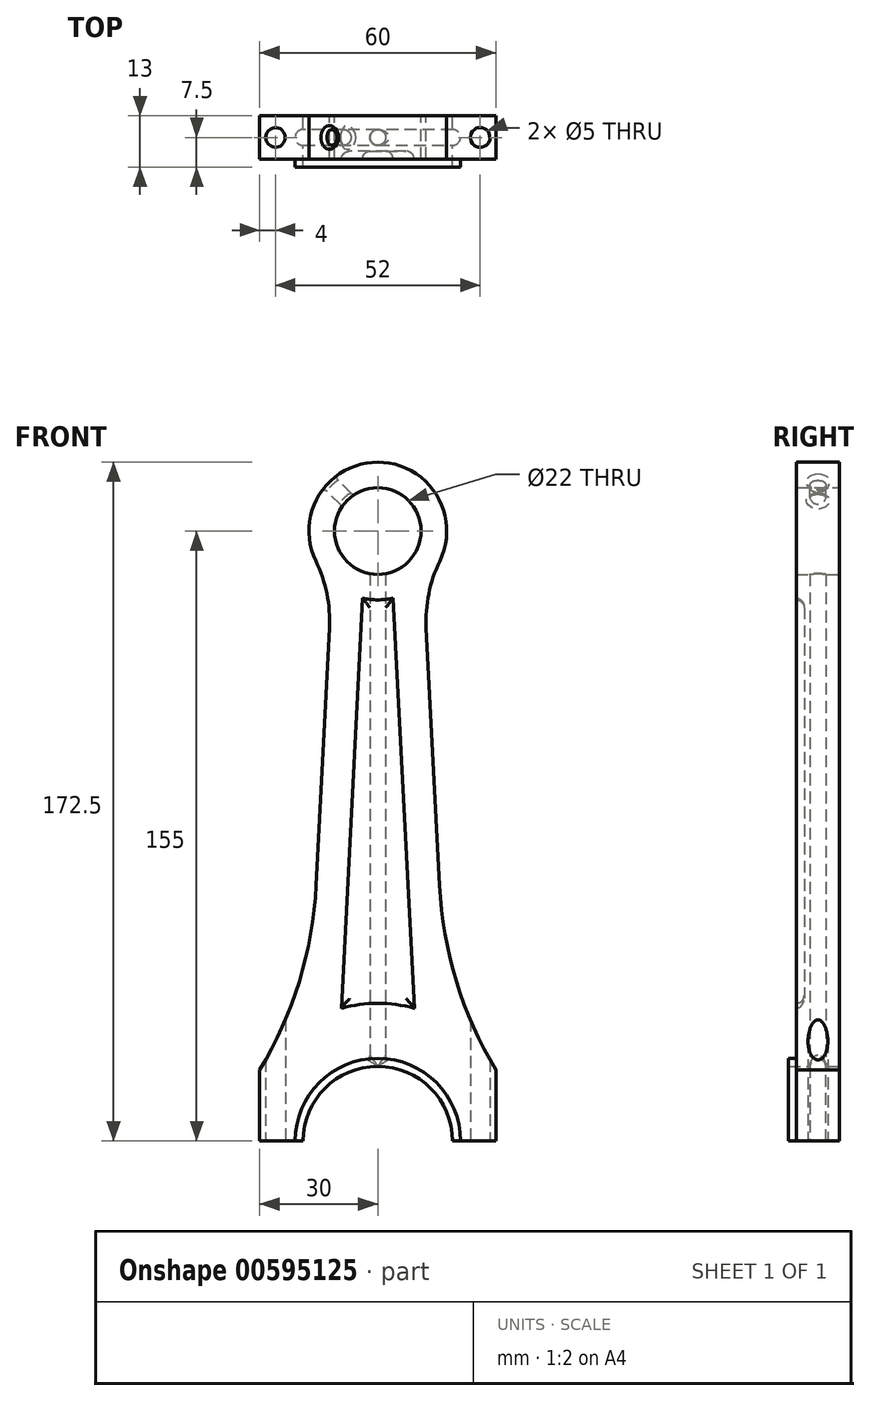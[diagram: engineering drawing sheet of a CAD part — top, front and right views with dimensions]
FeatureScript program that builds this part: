
annotation { "Feature Type Name" : "Feature", "Feature Type Description" : "" }
export const myFeature = defineFeature(function(context is Context, id is Id, definition is map)
    precondition{}
    {
        {
            var Q0;
            Q0=qCreatedBy(makeId("Front.planeOp"),FACE);
            var sketch = newSketch(context, id + "F0", { "sketchPlane" : qUnion([Q0])});
            skCircle(sketch, "E0", {"center": v(0, 77.5) * mm, "radius": 11 * mm});
            skArc(sketch, "E1", {"start": v(19, -77.5) * mm, "mid": v(0, -58.5) * mm, "end": v(-19, -77.5) * mm});
            skLineSegment(sketch, "E2", {"start": v(-12.3, 52.8) * mm, "end": v(-15.67, -12.54) * mm});
            skArc(sketch, "E3", {"start": v(15.75, 69.87) * mm, "mid": v(0, 95) * mm, "end": v(-15.75, 69.87) * mm});
            skLineSegment(sketch, "E4.trimOffspring", {"start": v(12.3, 52.8) * mm, "end": v(15.67, -12.54) * mm});
            skLineSegment(sketch, "E5", {"start": v(30, -59.47) * mm, "end": v(30, -77.5) * mm});
            skLineSegment(sketch, "E6.MirrorCS", {"start": v(-30, -59.47) * mm, "end": v(-30, -77.5) * mm});
            skLineSegment(sketch, "E7", {"start": v(0, -77.5) * mm, "end": v(-59.42, -77.5) * mm, "construction": true});
            skLineSegment(sketch, "E8.MirrorCS", {"start": v(0, -77.5) * mm, "end": v(59.42, -77.5) * mm, "construction": true});
            skLineSegment(sketch, "E9.trimOffspring", {"start": v(-30, -59.47) * mm, "end": v(-30, -59.47) * mm});
            skPoint(sketch, "E10.visualSharp", {"position": v(-17.46, -47.16) * mm});
            skArc(sketch, "E10.filletArc", {"start": v(-30, -59.47) * mm, "mid": v(-19.95, -36.89) * mm, "end": v(-15.67, -12.54) * mm});
            skArc(sketch, "E11.MirrorCS", {"start": v(30, -59.47) * mm, "mid": v(19.95, -36.89) * mm, "end": v(15.67, -12.54) * mm});
            skPoint(sketch, "E12.visualSharp", {"position": v(-11.69, 64.48) * mm});
            skArc(sketch, "E12.filletArc", {"start": v(-12.3, 52.8) * mm, "mid": v(-12.94, 61.55) * mm, "end": v(-15.75, 69.87) * mm});
            skPoint(sketch, "E13.visualSharp", {"position": v(11.69, 64.48) * mm});
            skArc(sketch, "E13.filletArc", {"start": v(15.75, 69.87) * mm, "mid": v(12.94, 61.55) * mm, "end": v(12.3, 52.8) * mm});
            skLineSegment(sketch, "E14", {"start": v(-30, -77.5) * mm, "end": v(-19, -77.5) * mm});
            skLineSegment(sketch, "E15", {"start": v(19, -77.5) * mm, "end": v(30, -77.5) * mm});
            skSolve(sketch);
        }
        {
            var Q0;
            Q0 = qSketchRegion(id + "F0", true);
            extrude(context, id + "F1", {"entities" : qUnion([Q0]), "endBound" : BoundingType.SYMMETRIC, "depth" : 11 * mm, "offsetDistance" : 25 * mm});
        }
        {
            var Q0;
            Q0=makeQuery(id+"F1.opExtrude","CAP_FACE",FACE,{"disambiguationData":[OSD([sQuery(id+"F0.wireOp",EDGE,"E0"),sQuery(id+"F0.wireOp",EDGE,"E1"),sQuery(id+"F0.wireOp",EDGE,"E2"),sQuery(id+"F0.wireOp",EDGE,"E3"),sQuery(id+"F0.wireOp",EDGE,"E4.trimOffspring"),sQuery(id+"F0.wireOp",EDGE,"E5"),sQuery(id+"F0.wireOp",EDGE,"E6.MirrorCS"),sQuery(id+"F0.wireOp",EDGE,"E10.filletArc"),sQuery(id+"F0.wireOp",EDGE,"E11.MirrorCS"),sQuery(id+"F0.wireOp",EDGE,"E12.filletArc"),sQuery(id+"F0.wireOp",EDGE,"E13.filletArc"),sQuery(id+"F0.wireOp",EDGE,"E14"),sQuery(id+"F0.wireOp",EDGE,"E15")])],"isStart":false});
            var sketch = newSketch(context, id + "F2", { "sketchPlane" : qUnion([Q0])});
            skLineSegment(sketch, "E16", {"start": v(3.88, 60.44) * mm, "end": v(9.26, -43.75) * mm});
            skLineSegment(sketch, "E17", {"start": v(0, 84.25) * mm, "end": v(0, -84.78) * mm, "construction": true});
            skPoint(sketch, "E17.endSnap0", {"position": v(0, -58.5) * mm});
            skLineSegment(sketch, "E18.MirrorCS", {"start": v(-3.88, 60.44) * mm, "end": v(-9.26, -43.75) * mm});
            skArc(sketch, "E19", {"start": v(-3.88, 60.44) * mm, "mid": v(0, 60) * mm, "end": v(3.88, 60.44) * mm});
            skArc(sketch, "E20", {"start": v(9.26, -43.75) * mm, "mid": v(0, -42.5) * mm, "end": v(-9.26, -43.75) * mm});
            skSolve(sketch);
        }
        {
            var Q0;
            Q0 = qSketchRegion(id + "F2", true);
            extrude(context, id + "F3", {"entities" : qUnion([Q0]), "operationType" : NewBodyOperationType.REMOVE, "oppositeDirection" : true, "depth" : 2 * mm, "offsetDistance" : 25 * mm});
        }
        {
            var Q0;
            Q0=makeQuery(id+"F1.opExtrude","SWEPT_FACE",FACE,{"disambiguationData":[OSD([sQuery(id+"F0.wireOp",EDGE,"E15")])]});
            var sketch = newSketch(context, id + "F4", { "sketchPlane" : qUnion([Q0])});
            skCircle(sketch, "E21", {"center": v(-26, 0) * mm, "radius": 2.5 * mm});
            skCircle(sketch, "E22", {"center": v(26, 0) * mm, "radius": 2.5 * mm});
            skSolve(sketch);
        }
        {
            var Q0;
            Q0 = qSketchRegion(id + "F4", true);
            extrude(context, id + "F5", {"entities" : qUnion([Q0]), "operationType" : NewBodyOperationType.REMOVE, "endBound" : BoundingType.THROUGH_ALL, "oppositeDirection" : true, "depth" : 25 * mm, "offsetDistance" : 25 * mm});
        }
        {
            var Q0;
            Q0=makeQuery(id+"F1.opExtrude","CAP_FACE",FACE,{"disambiguationData":[OSD([sQuery(id+"F0.wireOp",EDGE,"E0"),sQuery(id+"F0.wireOp",EDGE,"E1"),sQuery(id+"F0.wireOp",EDGE,"E2"),sQuery(id+"F0.wireOp",EDGE,"E3"),sQuery(id+"F0.wireOp",EDGE,"E4.trimOffspring"),sQuery(id+"F0.wireOp",EDGE,"E5"),sQuery(id+"F0.wireOp",EDGE,"E6.MirrorCS"),sQuery(id+"F0.wireOp",EDGE,"E10.filletArc"),sQuery(id+"F0.wireOp",EDGE,"E11.MirrorCS"),sQuery(id+"F0.wireOp",EDGE,"E12.filletArc"),sQuery(id+"F0.wireOp",EDGE,"E13.filletArc"),sQuery(id+"F0.wireOp",EDGE,"E14"),sQuery(id+"F0.wireOp",EDGE,"E15")])],"isStart":false});
            var sketch = newSketch(context, id + "F6", { "sketchPlane" : qUnion([Q0])});
            skArc(sketch, "E23", {"start": v(19, -77.5) * mm, "mid": v(0, -58.5) * mm, "end": v(-19, -77.5) * mm});
            skArc(sketch, "E24", {"start": v(21, -77.5) * mm, "mid": v(0, -56.5) * mm, "end": v(-21, -77.5) * mm});
            skLineSegment(sketch, "E25", {"start": v(-21, -77.5) * mm, "end": v(-19, -77.5) * mm});
            skLineSegment(sketch, "E26", {"start": v(19, -77.5) * mm, "end": v(21, -77.5) * mm});
            skSolve(sketch);
        }
        {
            var Q0;
            Q0 = qSketchRegion(id + "F6", true);
            extrude(context, id + "F7", {"entities" : qUnion([Q0]), "operationType" : NewBodyOperationType.ADD, "depth" : 2 * mm, "offsetDistance" : 25 * mm});
        }
        {
            var Q0;
            Q0=makeQuery(id+"F7.opExtrude","CAP_EDGE",EDGE,{"disambiguationData":[OSD([sQuery(id+"F6.wireOp",EDGE,"E24")])],"isStart":true});
            var Q1;
            Q1=makeQuery(id+"F3.boolean.opBoolean","COPY",EDGE,{"derivedFrom":makeQuery(id+"F3.opExtrude","CAP_EDGE",EDGE,{"disambiguationData":[OSD([sQuery(id+"F2.wireOp",EDGE,"E18.MirrorCS")])],"isStart":false})});
            var Q2;
            Q2=makeQuery(id+"F3.boolean.opBoolean","COPY",EDGE,{"derivedFrom":makeQuery(id+"F3.opExtrude","CAP_EDGE",EDGE,{"disambiguationData":[OSD([sQuery(id+"F2.wireOp",EDGE,"E20")])],"isStart":false})});
            var Q3;
            Q3=makeQuery(id+"F3.boolean.opBoolean","COPY",EDGE,{"derivedFrom":makeQuery(id+"F3.opExtrude","CAP_EDGE",EDGE,{"disambiguationData":[OSD([sQuery(id+"F2.wireOp",EDGE,"E16")])],"isStart":false})});
            var Q4;
            Q4=makeQuery(id+"F3.boolean.opBoolean","COPY",EDGE,{"derivedFrom":makeQuery(id+"F3.opExtrude","CAP_EDGE",EDGE,{"disambiguationData":[OSD([sQuery(id+"F2.wireOp",EDGE,"E19")])],"isStart":false})});
            var Q5;
            Q5=makeQuery(id+"FKdGpnk2Vj0JADh_1.1.F3.boolean.opBoolean","COPY",EDGE,{"derivedFrom":makeQuery(id+"FKdGpnk2Vj0JADh_1.1.F3.opExtrude","CAP_EDGE",EDGE,{"disambiguationData":[OSD([sQuery(id+"F2.wireOp",EDGE,"E20")])],"isStart":false})});
            var Q6;
            Q6=makeQuery(id+"FTUo5Aq20tstjSV_1.1.F7.opExtrude","CAP_EDGE",EDGE,{"disambiguationData":[OSD([sQuery(id+"F6.wireOp",EDGE,"E24")])],"isStart":true});
            var Q7;
            Q7=makeQuery(id+"FKdGpnk2Vj0JADh_1.1.F3.boolean.opBoolean","COPY",EDGE,{"derivedFrom":makeQuery(id+"FKdGpnk2Vj0JADh_1.1.F3.opExtrude","CAP_EDGE",EDGE,{"disambiguationData":[OSD([sQuery(id+"F2.wireOp",EDGE,"E16")])],"isStart":false})});
            var Q8;
            Q8=makeQuery(id+"FKdGpnk2Vj0JADh_1.1.F3.boolean.opBoolean","COPY",EDGE,{"derivedFrom":makeQuery(id+"FKdGpnk2Vj0JADh_1.1.F3.opExtrude","CAP_EDGE",EDGE,{"disambiguationData":[OSD([sQuery(id+"F2.wireOp",EDGE,"E19")])],"isStart":false})});
            var Q9;
            Q9=makeQuery(id+"FKdGpnk2Vj0JADh_1.1.F3.boolean.opBoolean","COPY",EDGE,{"derivedFrom":makeQuery(id+"FKdGpnk2Vj0JADh_1.1.F3.opExtrude","CAP_EDGE",EDGE,{"disambiguationData":[OSD([sQuery(id+"F2.wireOp",EDGE,"E18.MirrorCS")])],"isStart":false})});
            fillet(context, id + "F8", {"entities" : qUnion([Q0, Q1, Q2, Q3, Q4, Q5, Q6, Q7, Q8, Q9]), "radius" : 2 * mm, "tangentPropagation" : true, "allowEdgeOverflow" : false});
        }
        {
            var Q0;
            {var subQ0=sQuery(id+"F6.wireOp",EDGE,"E25");Q0=makeQuery(id+"FTUo5Aq20tstjSV_1.1.F7.boolean.opBoolean","MERGE",FACE,{"derivedFrom":[makeQuery(id+"F7.boolean.opBoolean","MERGE",FACE,{"derivedFrom":[makeQuery(id+"F1.opExtrude","SWEPT_FACE",FACE,{"disambiguationData":[OSD([sQuery(id+"F0.wireOp",EDGE,"E14")])]}),makeQuery(id+"F7.opExtrude","SWEPT_FACE",FACE,{"disambiguationData":[OSD([subQ0])]})]}),makeQuery(id+"FTUo5Aq20tstjSV_1.1.F7.opExtrude","SWEPT_FACE",FACE,{"disambiguationData":[OSD([subQ0])]})]});}
            var sketch = newSketch(context, id + "F9", { "sketchPlane" : qUnion([Q0])});
            skCircle(sketch, "E27", {"center": v(-19, 0) * mm, "radius": 2 * mm});
            skSolve(sketch);
        }
        {
            var Q0;
            Q0 = qSketchRegion(id + "F9", true);
            var Q1;
            {var subQ0=sQuery(id+"F6.wireOp",EDGE,"E23");Q1=makeQuery(id+"FTUo5Aq20tstjSV_1.1.F7.boolean.opBoolean","MERGE",FACE,{"derivedFrom":[makeQuery(id+"F7.boolean.opBoolean","MERGE",FACE,{"derivedFrom":[makeQuery(id+"F1.opExtrude","SWEPT_FACE",FACE,{"disambiguationData":[OSD([sQuery(id+"F0.wireOp",EDGE,"E1")])]}),makeQuery(id+"F7.opExtrude","SWEPT_FACE",FACE,{"disambiguationData":[OSD([subQ0])]})]}),makeQuery(id+"FTUo5Aq20tstjSV_1.1.F7.opExtrude","SWEPT_FACE",FACE,{"disambiguationData":[OSD([subQ0])]})]});}
            revolve(context, id + "F10", {"operationType" : NewBodyOperationType.REMOVE, "entities" : qUnion([Q0]), "axis" : qUnion([Q1]), "revolveType" : RevolveType.FULL, "oppositeDirection" : true});
        }
        {
            var Q0;
            {var subQ0=sQuery(id+"F6.wireOp",EDGE,"E25");Q0=makeQuery(id+"FTUo5Aq20tstjSV_1.1.F7.boolean.opBoolean","MERGE",FACE,{"derivedFrom":[makeQuery(id+"F7.boolean.opBoolean","MERGE",FACE,{"derivedFrom":[makeQuery(id+"F1.opExtrude","SWEPT_FACE",FACE,{"disambiguationData":[OSD([sQuery(id+"F0.wireOp",EDGE,"E14")])]}),makeQuery(id+"F7.opExtrude","SWEPT_FACE",FACE,{"disambiguationData":[OSD([subQ0])]})]}),makeQuery(id+"FTUo5Aq20tstjSV_1.1.F7.opExtrude","SWEPT_FACE",FACE,{"disambiguationData":[OSD([subQ0])]})]});}
            var sketch = newSketch(context, id + "F11", { "sketchPlane" : qUnion([Q0])});
            skCircle(sketch, "E28", {"center": v(0, 0) * mm, "radius": 2 * mm});
            skSolve(sketch);
        }
        {
            var Q0;
            Q0 = qSketchRegion(id + "F11", true);
            var Q1;
            Q1=makeQuery(id+"F1.opExtrude","SWEPT_FACE",FACE,{"disambiguationData":[OSD([sQuery(id+"F0.wireOp",EDGE,"E0")])]});
            extrude(context, id + "F12", {"entities" : qUnion([Q0]), "operationType" : NewBodyOperationType.REMOVE, "endBound" : BoundingType.UP_TO_SURFACE, "oppositeDirection" : true, "depth" : 25 * mm, "endBoundEntityFace" : qUnion([Q1]), "offsetDistance" : 25 * mm});
        }
        {
            var Q0;
            Q0=qCreatedBy(makeId("Front.planeOp"),FACE);
            var sketch = newSketch(context, id + "F13", { "sketchPlane" : qUnion([Q0])});
            skLineSegment(sketch, "E29", {"start": v(-49.97, 77.5) * mm, "end": v(56.86, 77.5) * mm, "construction": true});
            skCircle(sketch, "E30.0", {"center": v(0, 77.5) * mm, "radius": 11 * mm, "construction": true});
            skLineSegment(sketch, "E31", {"start": v(0, 77.5) * mm, "end": v(-36.47, 113.97) * mm, "construction": true});
            skLineSegment(sketch, "E32", {"start": v(-14.67, 92.17) * mm, "end": v(-13.25, 93.58) * mm});
            skLineSegment(sketch, "E33", {"start": v(-13.25, 93.58) * mm, "end": v(-3.22, 83.55) * mm});
            skLineSegment(sketch, "E34", {"start": v(-3.22, 83.55) * mm, "end": v(-4.63, 82.13) * mm});
            skLineSegment(sketch, "E35", {"start": v(-4.63, 82.13) * mm, "end": v(-14.67, 92.17) * mm});
            skSolve(sketch);
        }
        {
            var Q0;
            Q0 = qSketchRegion(id + "F13", true);
            var Q1;
            Q1=sQuery(id+"F13.wireOp",EDGE,"E31");
            revolve(context, id + "F14", {"operationType" : NewBodyOperationType.REMOVE, "entities" : qUnion([Q0]), "axis" : qUnion([Q1]), "revolveType" : RevolveType.FULL, "oppositeDirection" : true});
        }
        {
            var Q0;
            Q0=makeQuery(id+"F14.boolean.opBoolean","INTERSECT",EDGE,{"derivedFrom":[makeQuery(id+"F1.opExtrude","SWEPT_FACE",FACE,{"disambiguationData":[OSD([sQuery(id+"F0.wireOp",EDGE,"E3")])]}),makeQuery(id+"F14.opRevolve","SWEPT_FACE",FACE,{"disambiguationData":[OSD([sQuery(id+"F13.wireOp",EDGE,"E33")])]})]});
            var Q1;
            Q1=makeQuery(id+"FigsYOYNFft2UOf_1.1.F14.boolean.opBoolean","INTERSECT",EDGE,{"derivedFrom":[makeQuery(id+"F1.opExtrude","SWEPT_FACE",FACE,{"disambiguationData":[OSD([sQuery(id+"F0.wireOp",EDGE,"E3")])]}),makeQuery(id+"FigsYOYNFft2UOf_1.1.F14.opRevolve","SWEPT_FACE",FACE,{"disambiguationData":[OSD([sQuery(id+"F13.wireOp",EDGE,"E33")])]})]});
            var Q2;
            Q2=makeQuery(id+"F14.boolean.opBoolean","INTERSECT",EDGE,{"derivedFrom":[makeQuery(id+"F1.opExtrude","SWEPT_FACE",FACE,{"disambiguationData":[OSD([sQuery(id+"F0.wireOp",EDGE,"E0")])]}),makeQuery(id+"F14.opRevolve","SWEPT_FACE",FACE,{"disambiguationData":[OSD([sQuery(id+"F13.wireOp",EDGE,"E33")])]})]});
            var Q3;
            Q3=makeQuery(id+"FigsYOYNFft2UOf_1.1.F14.boolean.opBoolean","INTERSECT",EDGE,{"derivedFrom":[makeQuery(id+"F1.opExtrude","SWEPT_FACE",FACE,{"disambiguationData":[OSD([sQuery(id+"F0.wireOp",EDGE,"E0")])]}),makeQuery(id+"FigsYOYNFft2UOf_1.1.F14.opRevolve","SWEPT_FACE",FACE,{"disambiguationData":[OSD([sQuery(id+"F13.wireOp",EDGE,"E33")])]})]});
            var Q4;
            Q4=makeQuery(id+"F12.boolean.opBoolean","COPY",EDGE,{"derivedFrom":makeQuery(id+"F12.opExtrude","CAP_EDGE",EDGE,{"disambiguationData":[OSD([sQuery(id+"F11.wireOp",EDGE,"E28")])],"isStart":false})});
            var Q5;
            Q5=makeQuery(id+"F12.boolean.opBoolean","INTERSECT",EDGE,{"disambiguationData":[OD(0.0)],"derivedFrom":[makeQuery(id+"F10.boolean.opBoolean","COPY",FACE,{"derivedFrom":makeQuery(id+"F10.opRevolve","SWEPT_FACE",FACE,{"disambiguationData":[OSD([sQuery(id+"F9.wireOp",EDGE,"E27")])]})}),makeQuery(id+"F12.opExtrude","SWEPT_FACE",FACE,{"disambiguationData":[OSD([sQuery(id+"F11.wireOp",EDGE,"E28")])]})]});
            var Q6;
            Q6=makeQuery(id+"F12.boolean.opBoolean","INTERSECT",EDGE,{"disambiguationData":[OD(1.0)],"derivedFrom":[makeQuery(id+"F10.boolean.opBoolean","COPY",FACE,{"derivedFrom":makeQuery(id+"F10.opRevolve","SWEPT_FACE",FACE,{"disambiguationData":[OSD([sQuery(id+"F9.wireOp",EDGE,"E27")])]})}),makeQuery(id+"F12.opExtrude","SWEPT_FACE",FACE,{"disambiguationData":[OSD([sQuery(id+"F11.wireOp",EDGE,"E28")])]})]});
            fillet(context, id + "F15", {"entities" : qUnion([Q0, Q1, Q2, Q3, Q4, Q5, Q6]), "radius" : 1 * mm, "tangentPropagation" : true, "allowEdgeOverflow" : false});
        }
    });
